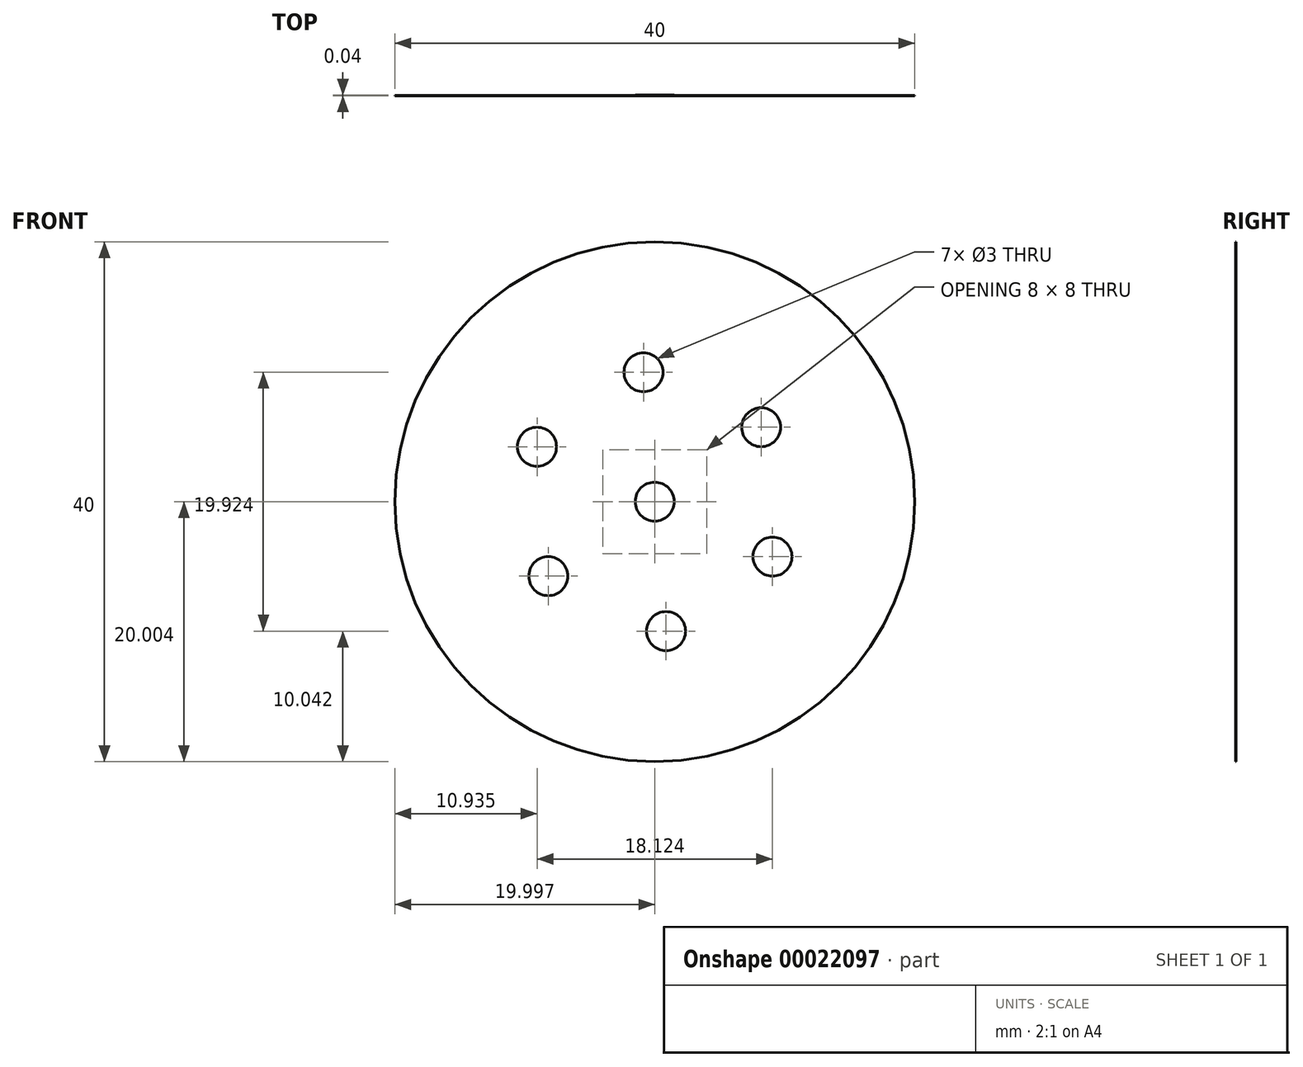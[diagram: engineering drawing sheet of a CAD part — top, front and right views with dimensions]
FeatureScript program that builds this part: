
annotation { "Feature Type Name" : "Feature", "Feature Type Description" : "" }
export const myFeature = defineFeature(function(context is Context, id is Id, definition is map)
    precondition{}
    {
        {
            var Q0;
            Q0=qCreatedBy(makeId("Front.planeOp"),FACE);
            var sketch = newSketch(context, id + "F0", { "sketchPlane" : qUnion([Q0])});
            skCircle(sketch, "E0", {"center": v(13.4, 32.62) * mm, "radius": 20 * mm});
            skCircle(sketch, "E1", {"center": v(13.4, 32.62) * mm, "radius": 1.5 * mm});
            skCircle(sketch, "E2", {"center": v(13.4, 32.62) * mm, "radius": 4 * mm});
            skCircle(sketch, "E3", {"center": v(4.34, 36.85) * mm, "radius": 1.5 * mm});
            skCircle(sketch, "E4.1.0", {"center": v(5.2, 26.9) * mm, "radius": 1.5 * mm});
            skCircle(sketch, "E4.2.0", {"center": v(14.27, 22.66) * mm, "radius": 1.5 * mm});
            skCircle(sketch, "E4.3.0", {"center": v(22.46, 28.4) * mm, "radius": 1.5 * mm});
            skCircle(sketch, "E4.4.0", {"center": v(21.6, 38.36) * mm, "radius": 1.5 * mm});
            skCircle(sketch, "E4.5.0", {"center": v(12.53, 42.59) * mm, "radius": 1.5 * mm});
            skSolve(sketch);
        }
        {
            var Q0;
            Q0=makeQuery(id+"F0.imprint","IMPRINT",FACE,{"disambiguationData":[TD([[makeQuery(id+"F0.imprint","IMPRINT",EDGE,{"derivedFrom":sQuery(id+"F0.wireOp",EDGE,"E1")}),-1.0]])]});
            extrude(context, id + "F1", {"entities" : qUnion([Q0]), "endBound" : BoundingType.SYMMETRIC, "depth" : 4 / 100 * mm});
        }
        {
            var Q0;
            Q0=makeQuery(id+"F0.imprint","IMPRINT",FACE,{"disambiguationData":[TD([[makeQuery(id+"F0.imprint","IMPRINT",EDGE,{"derivedFrom":sQuery(id+"F0.wireOp",EDGE,"E0")}),1.0]])]});
            extrude(context, id + "F2", {"entities" : qUnion([Q0]), "operationType" : NewBodyOperationType.ADD, "endBound" : BoundingType.SYMMETRIC, "depth" : 3 / 100 * mm});
        }
    });
